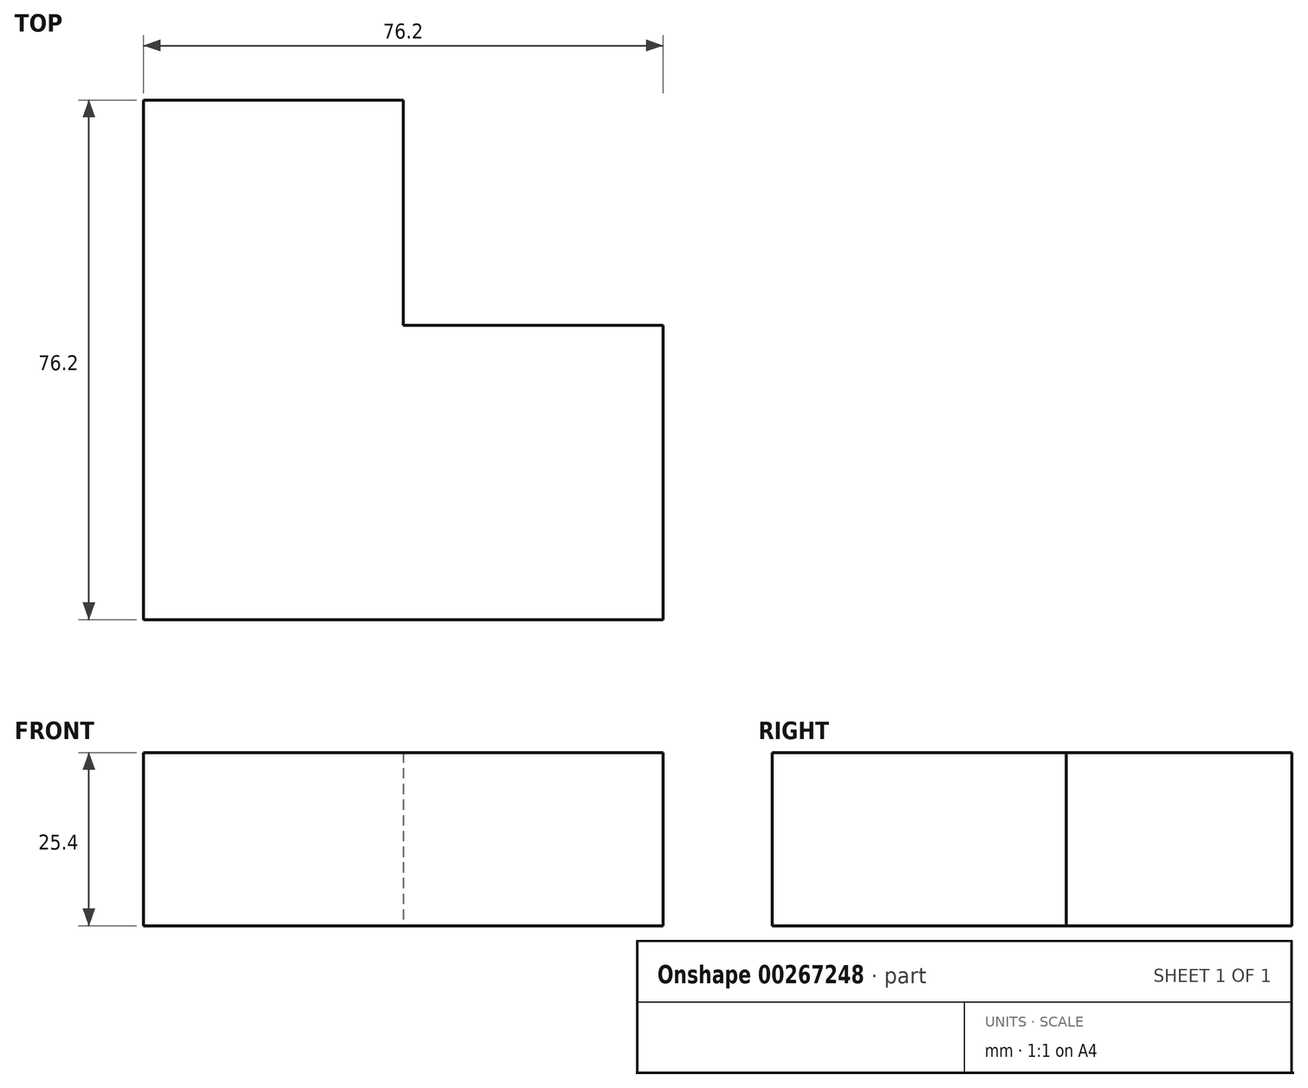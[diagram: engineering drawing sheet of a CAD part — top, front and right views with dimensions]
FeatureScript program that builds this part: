
annotation { "Feature Type Name" : "Feature", "Feature Type Description" : "" }
export const myFeature = defineFeature(function(context is Context, id is Id, definition is map)
    precondition{}
    {
        {
            var Q0;
            Q0=qCreatedBy(makeId("Top.planeOp"),FACE);
            var sketch = newSketch(context, id + "F0", { "sketchPlane" : qUnion([Q0])});
            skLineSegment(sketch, "E0.bottom", {"start": v(0, 0) * mm, "end": v(38.1, 0) * mm});
            skLineSegment(sketch, "E0.top", {"start": v(0, -76.2) * mm, "end": v(76.2, -76.2) * mm});
            skLineSegment(sketch, "E0.left", {"start": v(0, 0) * mm, "end": v(0, -76.2) * mm});
            skLineSegment(sketch, "E0.right", {"start": v(76.2, -33.07) * mm, "end": v(76.2, -76.2) * mm});
            skLineSegment(sketch, "E1", {"start": v(38.1, 0) * mm, "end": v(38.1, -33.07) * mm});
            skLineSegment(sketch, "E2", {"start": v(38.1, -33.07) * mm, "end": v(76.2, -33.07) * mm});
            skPoint(sketch, "E2.endSnap0", {"position": v(76.2, -38.1) * mm});
            skPoint(sketch, "E3.orphan", {"position": v(76.2, 0) * mm});
            skSolve(sketch);
        }
        {
            var Q0;
            Q0=makeQuery(id+"F0.imprint","IMPRINT",FACE,{"disambiguationData":[TD([[makeQuery(id+"F0.imprint","IMPRINT",EDGE,{"derivedFrom":sQuery(id+"F0.wireOp",EDGE,"E0.bottom")}),-1.0]])]});
            extrude(context, id + "F1", {"entities" : qUnion([Q0]), "depth" : 25.4 * mm});
        }
    });
